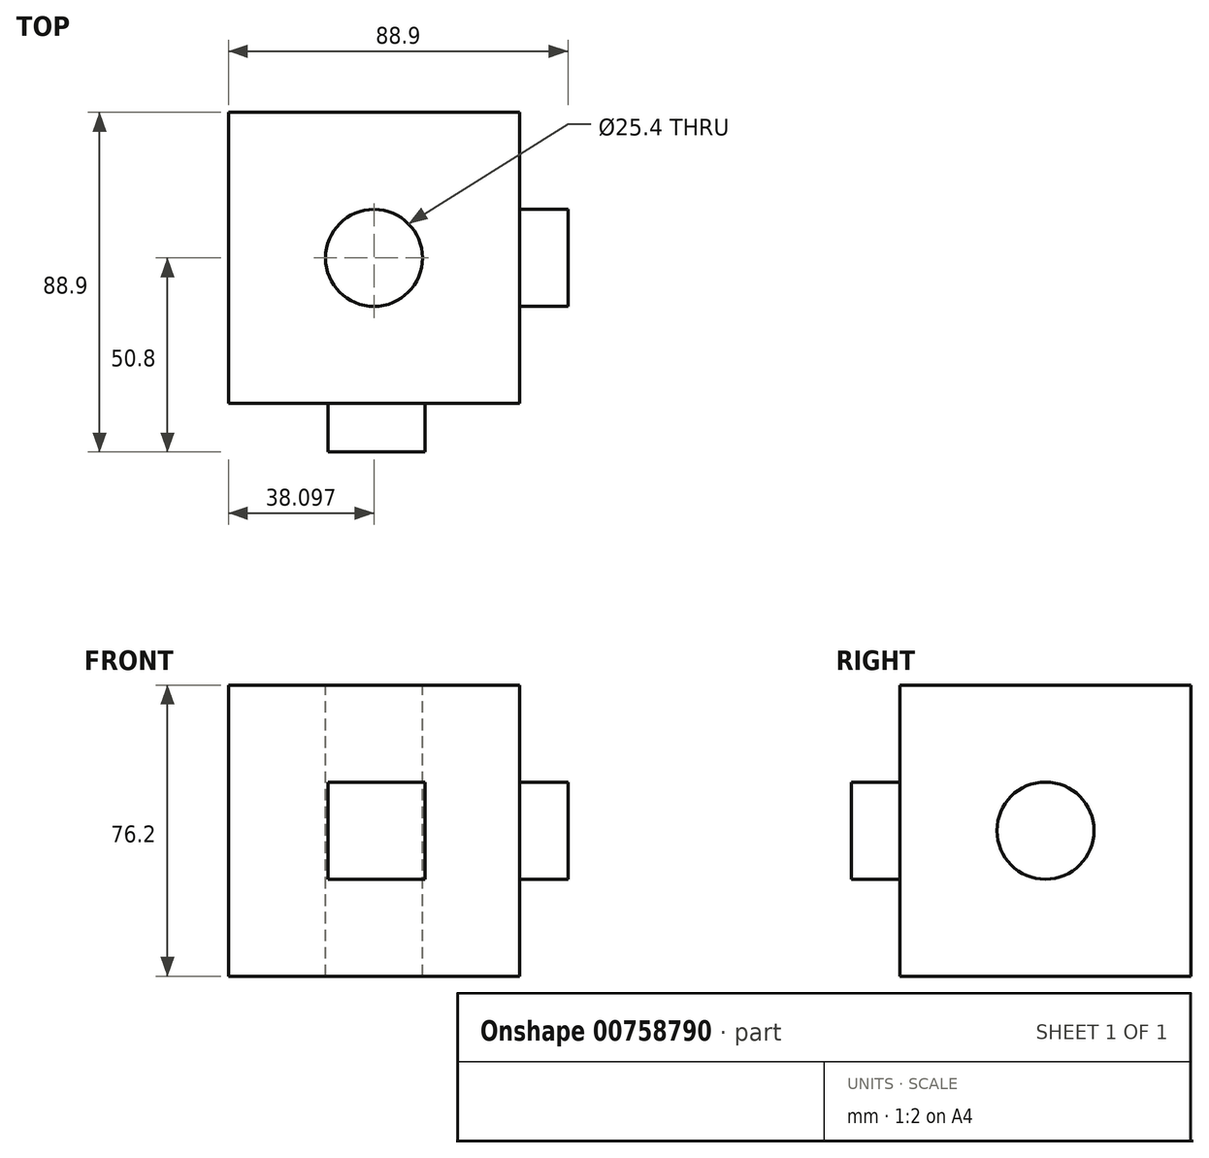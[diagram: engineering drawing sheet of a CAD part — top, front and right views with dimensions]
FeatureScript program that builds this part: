
annotation { "Feature Type Name" : "Feature", "Feature Type Description" : "" }
export const myFeature = defineFeature(function(context is Context, id is Id, definition is map)
    precondition{}
    {
        {
            var Q0;
            Q0=qCreatedBy(makeId("Front.planeOp"),FACE);
            var sketch = newSketch(context, id + "F0", { "sketchPlane" : qUnion([Q0])});
            skLineSegment(sketch, "E0.bottom", {"start": v(30.44, 29.5) * mm, "end": v(-45.76, 29.5) * mm});
            skLineSegment(sketch, "E0.top", {"start": v(30.44, -46.7) * mm, "end": v(-45.76, -46.7) * mm});
            skLineSegment(sketch, "E0.left", {"start": v(30.44, 29.5) * mm, "end": v(30.44, -46.7) * mm});
            skLineSegment(sketch, "E0.right", {"start": v(-45.76, 29.5) * mm, "end": v(-45.76, -46.7) * mm});
            skSolve(sketch);
        }
        {
            var Q0;
            Q0=makeQuery(id+"F0.imprint","IMPRINT",FACE,{"disambiguationData":[TD([[makeQuery(id+"F0.imprint","IMPRINT",EDGE,{"derivedFrom":sQuery(id+"F0.wireOp",EDGE,"E0.bottom")}),1.0]])]});
            extrude(context, id + "F1", {"entities" : qUnion([Q0]), "depth" : 76.2 * mm, "offsetDistance" : 25.4 * mm});
        }
        {
            var Q0;
            Q0=makeQuery(id+"F1.opExtrude","CAP_FACE",FACE,{"disambiguationData":[OSD([sQuery(id+"F0.wireOp",EDGE,"E0.bottom"),sQuery(id+"F0.wireOp",EDGE,"E0.top"),sQuery(id+"F0.wireOp",EDGE,"E0.left"),sQuery(id+"F0.wireOp",EDGE,"E0.right")])],"isStart":false});
            var sketch = newSketch(context, id + "F2", { "sketchPlane" : qUnion([Q0])});
            skLineSegment(sketch, "E1.bottom", {"start": v(5.67, 4.1) * mm, "end": v(-19.73, 4.1) * mm});
            skLineSegment(sketch, "E1.top", {"start": v(5.67, -21.3) * mm, "end": v(-19.73, -21.3) * mm});
            skLineSegment(sketch, "E1.left", {"start": v(5.67, 4.1) * mm, "end": v(5.67, -21.3) * mm});
            skLineSegment(sketch, "E1.right", {"start": v(-19.73, 4.1) * mm, "end": v(-19.73, -21.3) * mm});
            skSolve(sketch);
        }
        {
            var Q0;
            Q0=makeQuery(id+"F2.imprint","IMPRINT",FACE,{"disambiguationData":[TD([[makeQuery(id+"F2.imprint","IMPRINT",EDGE,{"derivedFrom":sQuery(id+"F2.wireOp",EDGE,"E1.bottom")}),1.0]])]});
            extrude(context, id + "F3", {"entities" : qUnion([Q0]), "operationType" : NewBodyOperationType.ADD, "depth" : 12.7 * mm, "offsetDistance" : 25.4 * mm});
        }
        {
            var Q0;
            Q0=makeQuery(id+"F1.opExtrude","SWEPT_FACE",FACE,{"disambiguationData":[OSD([sQuery(id+"F0.wireOp",EDGE,"E0.left")])]});
            var sketch = newSketch(context, id + "F4", { "sketchPlane" : qUnion([Q0])});
            skCircle(sketch, "E2", {"center": v(-38.1, -8.6) * mm, "radius": 12.7 * mm});
            skSolve(sketch);
        }
        {
            var Q0;
            Q0=makeQuery(id+"F4.imprint","IMPRINT",FACE,{"disambiguationData":[TD([[makeQuery(id+"F4.imprint","IMPRINT",EDGE,{"derivedFrom":sQuery(id+"F4.wireOp",EDGE,"E2")}),1.0]])]});
            extrude(context, id + "F5", {"entities" : qUnion([Q0]), "operationType" : NewBodyOperationType.ADD, "depth" : 12.7 * mm, "offsetDistance" : 25.4 * mm});
        }
        {
            var Q0;
            Q0=makeQuery(id+"F1.opExtrude","SWEPT_FACE",FACE,{"disambiguationData":[OSD([sQuery(id+"F0.wireOp",EDGE,"E0.bottom")])]});
            var sketch = newSketch(context, id + "F6", { "sketchPlane" : qUnion([Q0])});
            skPoint(sketch, "E3", {"position": v(-7.66, -38.1) * mm});
            skSolve(sketch);
        }
        {
            var Q0;
            Q0=sQuery(id+"F6.wireOp",VERTEX,"E3");
            var Q1;
            Q1=makeQuery(id+"F1.opExtrude","SWEPT_BODY",BODY,{"disambiguationData":[OSD([sQuery(id+"F0.wireOp",EDGE,"E0.bottom"),sQuery(id+"F0.wireOp",EDGE,"E0.top"),sQuery(id+"F0.wireOp",EDGE,"E0.left"),sQuery(id+"F0.wireOp",EDGE,"E0.right")])]});
            hole(context, id + "F7", {"style" : HoleStyle.SIMPLE, "endStyle" : HoleEndStyle.THROUGH, "holeDiameter" : 25.4 * mm, "majorDiameter" : 6.35 * mm, "isTappedThrough" : true, "tappedDepth" : 12.7 * mm, "tapClearance" : 3, "locations" : qUnion([Q0]), "scope" : qUnion([Q1])});
        }
    });
